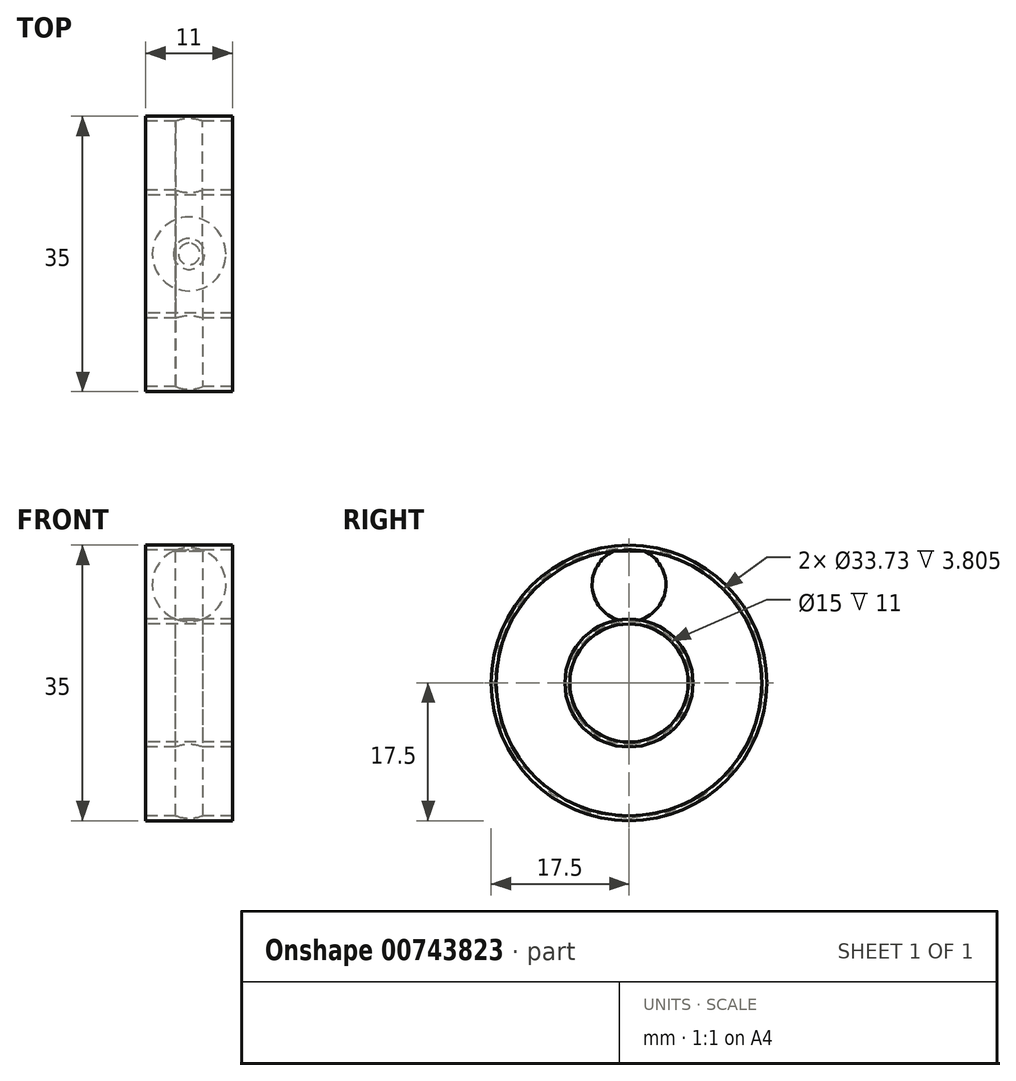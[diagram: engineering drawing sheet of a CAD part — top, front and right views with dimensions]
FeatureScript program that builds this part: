
annotation { "Feature Type Name" : "Feature", "Feature Type Description" : "" }
export const myFeature = defineFeature(function(context is Context, id is Id, definition is map)
    precondition{}
    {
        {
            var Q0;
            Q0=qCreatedBy(makeId("Right.planeOp"),FACE);
            var sketch = newSketch(context, id + "F0", { "sketchPlane" : qUnion([Q0])});
            skCircle(sketch, "E0", {"center": v(0, 0) * mm, "radius": 7.5 * mm});
            skCircle(sketch, "E1", {"center": v(0, 0) * mm, "radius": 8.13 * mm});
            skCircle(sketch, "E2", {"center": v(0, 0) * mm, "radius": 16.87 * mm});
            skCircle(sketch, "E3", {"center": v(0, 0) * mm, "radius": 17.5 * mm});
            skLineSegment(sketch, "E4", {"start": v(0, 8.13) * mm, "end": v(0, 12.5) * mm});
            skLineSegment(sketch, "E5", {"start": v(0, 12.5) * mm, "end": v(0, 16.87) * mm});
            skCircle(sketch, "E6", {"center": v(0, 12.5) * mm, "radius": 4.68 * mm});
            skSolve(sketch);
        }
        {
            var Q0;
            Q0=makeQuery(id+"F0.imprint","IMPRINT",FACE,{"disambiguationData":[TD([[makeQuery(id+"F0.imprint","IMPRINT",EDGE,{"derivedFrom":sQuery(id+"F0.wireOp",EDGE,"E0")}),-1.0]])]});
            var Q1;
            {var subQ0=sQuery(id+"F0.wireOp",EDGE,"E1");var subQ1=makeQuery(id+"F0.imprint","INTERSECT",VERTEX,{"derivedFrom":[subQ0,sQuery(id+"F0.wireOp",EDGE,"E4")]});Q1=makeQuery(id+"F0.imprint","IMPRINT",FACE,{"disambiguationData":[TD([[makeQuery(id+"F0.imprint","IMPRINT",EDGE,{"disambiguationData":[TD([[subQ1,1.0]])],"derivedFrom":subQ0}),1.0]])]});}
            var Q2;
            Q2=makeQuery(id+"F0.imprint","IMPRINT",FACE,{"disambiguationData":[TD([[makeQuery(id+"F0.imprint","IMPRINT",EDGE,{"derivedFrom":sQuery(id+"F0.wireOp",EDGE,"E3")}),1.0]])]});
            var Q3;
            {var subQ0=sQuery(id+"F0.wireOp",EDGE,"E2");var subQ1=makeQuery(id+"F0.imprint","INTERSECT",VERTEX,{"derivedFrom":[subQ0,sQuery(id+"F0.wireOp",EDGE,"E5")]});Q3=makeQuery(id+"F0.imprint","IMPRINT",FACE,{"disambiguationData":[TD([[makeQuery(id+"F0.imprint","IMPRINT",EDGE,{"disambiguationData":[TD([[subQ1,1.0]])],"derivedFrom":subQ0}),-1.0]])]});}
            extrude(context, id + "F1", {"entities" : qUnion([Q0, Q1, Q2, Q3]), "endBound" : BoundingType.SYMMETRIC, "depth" : 11 * mm, "offsetDistance" : 25.4 * mm});
        }
        {
            var Q0;
            Q0=qCreatedBy(makeId("Front.planeOp"),FACE);
            var sketch = newSketch(context, id + "F2", { "sketchPlane" : qUnion([Q0])});
            skPoint(sketch, "E7", {"position": v(0, 12.5) * mm});
            skPoint(sketch, "E8", {"position": v(0, 17.18) * mm});
            skPoint(sketch, "E9", {"position": v(0, 7.82) * mm});
            skLineSegment(sketch, "E10", {"start": v(0, 17.18) * mm, "end": v(0, 12.5) * mm});
            skLineSegment(sketch, "E11", {"start": v(0, 12.5) * mm, "end": v(0, 7.82) * mm});
            skCircle(sketch, "E12", {"center": v(0, 12.5) * mm, "radius": 4.68 * mm});
            skSolve(sketch);
        }
        {
            var Q0;
            {var subQ0=sQuery(id+"F2.wireOp",EDGE,"E10");Q0=makeQuery(id+"F2.imprint","IMPRINT",FACE,{"disambiguationData":[TD([[makeQuery(id+"F2.imprint","IMPRINT",EDGE,{"derivedFrom":subQ0}),1.0]])]});}
            var Q1;
            {var subQ0=sQuery(id+"F2.wireOp",EDGE,"E10");Q1=makeQuery(id+"F2.imprint","IMPRINT",FACE,{"disambiguationData":[TD([[makeQuery(id+"F2.imprint","IMPRINT",EDGE,{"derivedFrom":subQ0}),-1.0]])]});}
            var Q2;
            Q2=makeQuery(id+"F1.opExtrude","SWEPT_FACE",FACE,{"disambiguationData":[OSD([sQuery(id+"F0.wireOp",EDGE,"E0")])]});
            revolve(context, id + "F3", {"operationType" : NewBodyOperationType.REMOVE, "surfaceOperationType" : NewSurfaceOperationType.NEW, "entities" : qUnion([Q0, Q1]), "axis" : qUnion([Q2]), "revolveType" : RevolveType.FULL, "oppositeDirection" : true});
        }
        {
            var Q0;
            {var subQ0=sQuery(id+"F0.wireOp",EDGE,"E4");Q0=makeQuery(id+"F0.imprint","IMPRINT",FACE,{"disambiguationData":[TD([[makeQuery(id+"F0.imprint","IMPRINT",EDGE,{"derivedFrom":subQ0}),-1.0]])]});}
            var Q1;
            Q1=sQuery(id+"F0.wireOp",EDGE,"E5");
            revolve(context, id + "F4", {"surfaceOperationType" : NewSurfaceOperationType.NEW, "entities" : qUnion([Q0]), "axis" : qUnion([Q1]), "revolveType" : RevolveType.FULL});
        }
    });
